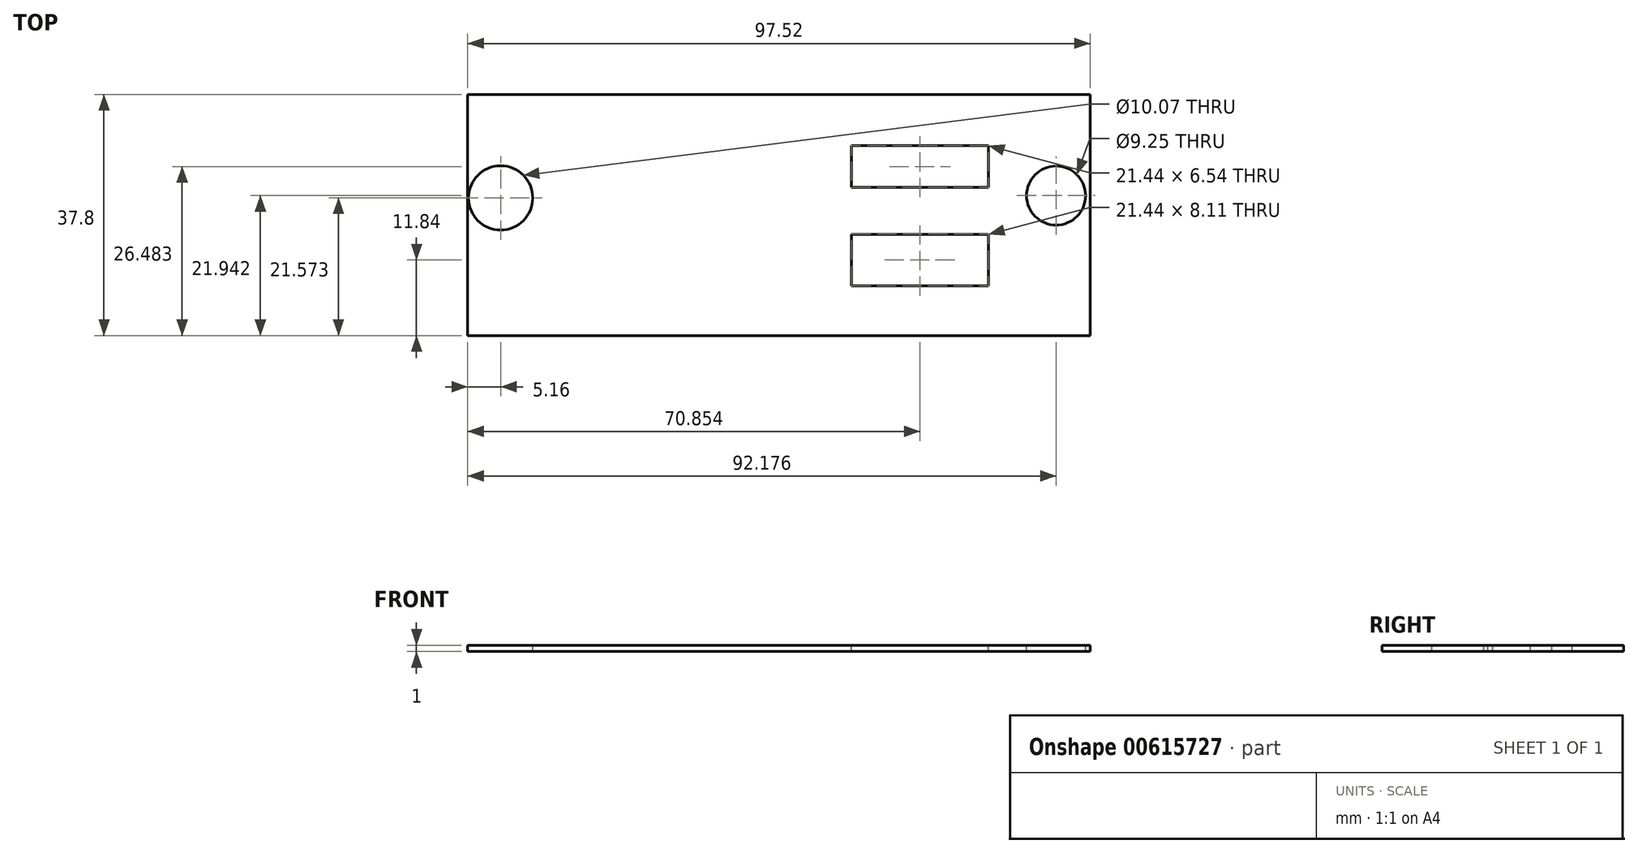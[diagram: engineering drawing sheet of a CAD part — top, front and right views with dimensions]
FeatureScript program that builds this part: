
annotation { "Feature Type Name" : "Feature", "Feature Type Description" : "" }
export const myFeature = defineFeature(function(context is Context, id is Id, definition is map)
    precondition{}
    {
        {
            var Q0;
            Q0=qCreatedBy(makeId("Top.planeOp"),FACE);
            var sketch = newSketch(context, id + "F0", { "sketchPlane" : qUnion([Q0])});
            skLineSegment(sketch, "E0.bottom", {"start": v(-48.76, 18.9) * mm, "end": v(48.76, 18.9) * mm});
            skLineSegment(sketch, "E0.top", {"start": v(-48.76, -18.9) * mm, "end": v(48.76, -18.9) * mm});
            skLineSegment(sketch, "E0.left", {"start": v(-48.76, 18.9) * mm, "end": v(-48.76, -18.9) * mm});
            skLineSegment(sketch, "E0.right", {"start": v(48.76, 18.9) * mm, "end": v(48.76, -18.9) * mm});
            skPoint(sketch, "E0.middle", {"position": v(0, 0) * mm});
            skSolve(sketch);
        }
        {
            var Q0;
            Q0 = qSketchRegion(id + "F0", true);
            extrude(context, id + "F1", {"entities" : qUnion([Q0]), "depth" : 1 * mm, "offsetDistance" : 25.4 * mm});
        }
        {
            var Q0;
            Q0=makeQuery(id+"F1.opExtrude","CAP_FACE",FACE,{"disambiguationData":[OSD([sQuery(id+"F0.wireOp",EDGE,"E0.bottom"),sQuery(id+"F0.wireOp",EDGE,"E0.top"),sQuery(id+"F0.wireOp",EDGE,"E0.left"),sQuery(id+"F0.wireOp",EDGE,"E0.right")])],"isStart":false});
            var sketch = newSketch(context, id + "F2", { "sketchPlane" : qUnion([Q0])});
            skCircle(sketch, "E1", {"center": v(43.42, 3.04) * mm, "radius": 4.62 * mm});
            skCircle(sketch, "E2", {"center": v(-43.6, 2.67) * mm, "radius": 5.04 * mm});
            skSolve(sketch);
        }
        {
            var Q0;
            Q0 = qSketchRegion(id + "F2", true);
            extrude(context, id + "F3", {"entities" : qUnion([Q0]), "operationType" : NewBodyOperationType.REMOVE, "oppositeDirection" : true, "depth" : 25.4 * mm, "offsetDistance" : 25.4 * mm});
        }
        {
            var Q0;
            Q0=makeQuery(id+"F1.opExtrude","CAP_FACE",FACE,{"disambiguationData":[OSD([sQuery(id+"F0.wireOp",EDGE,"E0.bottom"),sQuery(id+"F0.wireOp",EDGE,"E0.top"),sQuery(id+"F0.wireOp",EDGE,"E0.left"),sQuery(id+"F0.wireOp",EDGE,"E0.right")])],"isStart":false});
            var sketch = newSketch(context, id + "F4", { "sketchPlane" : qUnion([Q0])});
            skLineSegment(sketch, "E3", {"start": v(32.81, 10.85) * mm, "end": v(11.37, 10.85) * mm});
            skLineSegment(sketch, "E4", {"start": v(11.37, 10.85) * mm, "end": v(11.37, 4.31) * mm});
            skLineSegment(sketch, "E5", {"start": v(13.99, 4.31) * mm, "end": v(32.81, 4.31) * mm});
            skLineSegment(sketch, "E6", {"start": v(32.81, 4.31) * mm, "end": v(11.37, 4.31) * mm});
            skLineSegment(sketch, "E7", {"start": v(32.81, 4.31) * mm, "end": v(32.81, 10.85) * mm});
            skLineSegment(sketch, "E8", {"start": v(32.81, -3) * mm, "end": v(11.37, -3) * mm});
            skPoint(sketch, "E8.startSnap0", {"position": v(32.81, 7.58) * mm});
            skLineSegment(sketch, "E9", {"start": v(11.37, -3) * mm, "end": v(11.37, -11.11) * mm});
            skLineSegment(sketch, "E10", {"start": v(11.37, -11.11) * mm, "end": v(32.81, -11.11) * mm});
            skLineSegment(sketch, "E11", {"start": v(32.81, -11.11) * mm, "end": v(32.81, -3) * mm});
            skSolve(sketch);
        }
        {
            var Q0;
            Q0 = qSketchRegion(id + "F4", true);
            extrude(context, id + "F5", {"entities" : qUnion([Q0]), "operationType" : NewBodyOperationType.REMOVE, "oppositeDirection" : true, "depth" : 25.4 * mm, "offsetDistance" : 25.4 * mm});
        }
    });
